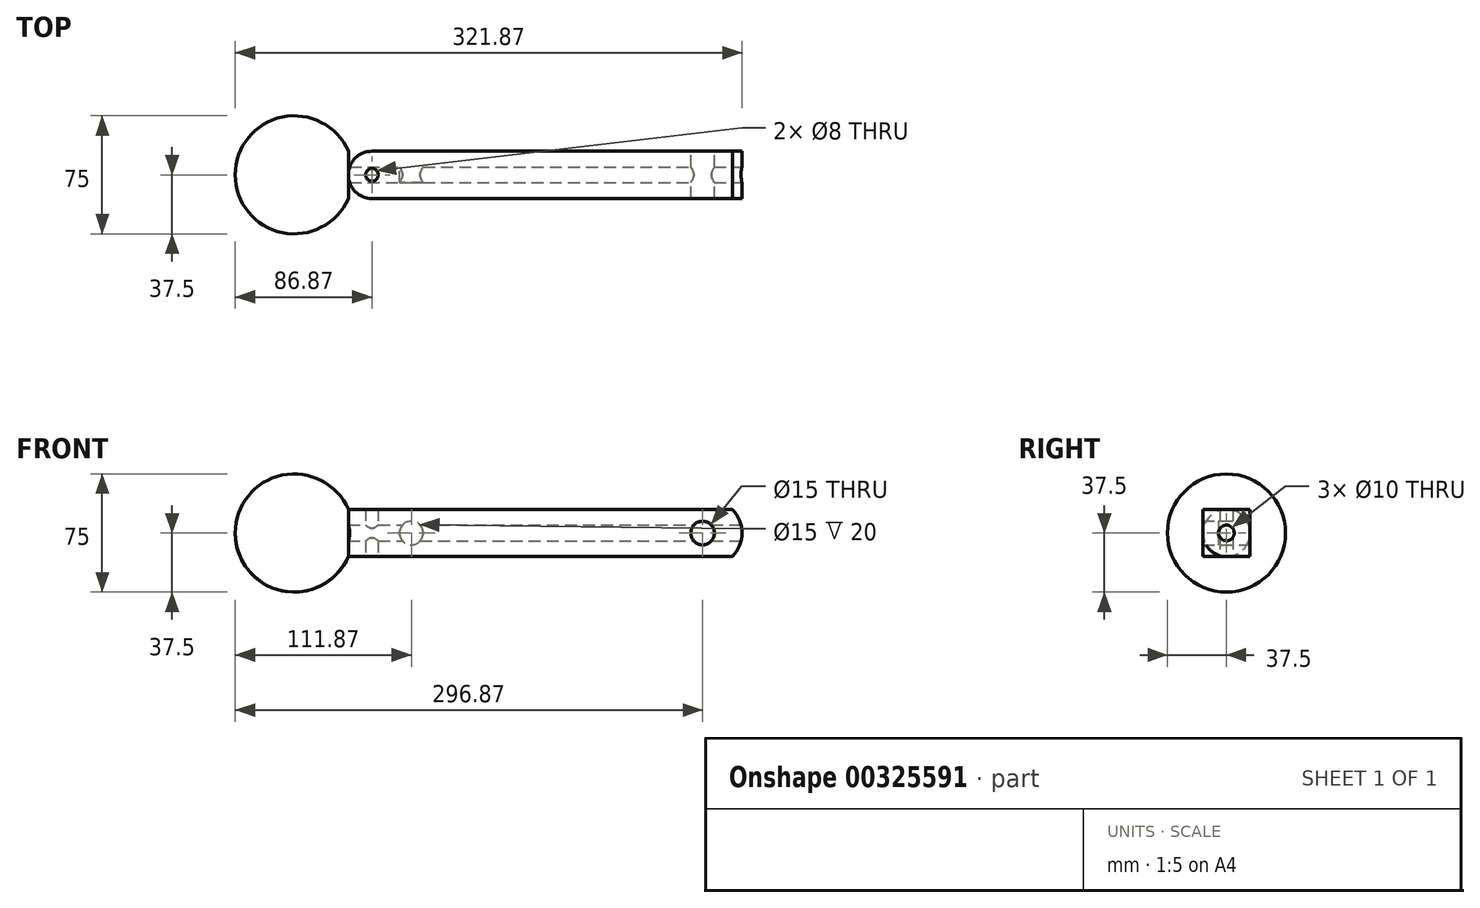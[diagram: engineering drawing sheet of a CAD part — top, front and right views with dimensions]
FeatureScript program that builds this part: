
annotation { "Feature Type Name" : "Feature", "Feature Type Description" : "" }
export const myFeature = defineFeature(function(context is Context, id is Id, definition is map)
    precondition{}
    {
        {
            var Q0;
            Q0=qCreatedBy(makeId("Right.planeOp"),FACE);
            var sketch = newSketch(context, id + "F0", { "sketchPlane" : qUnion([Q0])});
            skLineSegment(sketch, "E0.bottom", {"start": v(15, -15) * mm, "end": v(-15, -15) * mm});
            skLineSegment(sketch, "E0.top", {"start": v(15, 15) * mm, "end": v(-15, 15) * mm});
            skLineSegment(sketch, "E0.left", {"start": v(15, -15) * mm, "end": v(15, 15) * mm});
            skLineSegment(sketch, "E0.right", {"start": v(-15, -15) * mm, "end": v(-15, 15) * mm});
            skPoint(sketch, "E0.middle", {"position": v(0, 0) * mm});
            skSolve(sketch);
        }
        {
            var Q0;
            Q0=makeQuery(id+"F0.imprint","IMPRINT",FACE,{"disambiguationData":[TD([[makeQuery(id+"F0.imprint","IMPRINT",EDGE,{"derivedFrom":sQuery(id+"F0.wireOp",EDGE,"E0.bottom")}),-1.0]])]});
            var Q1;
            Q1 = qConstructionFilter(qBodyType(qCreatedBy(id + "F0" ,EDGE), BodyType.WIRE), ConstructionObject.NO);
            extrude(context, id + "F1", {"entities" : qUnion([Q0]), "surfaceEntities" : qUnion([Q1]), "depth" : 250 * mm});
        }
        {
            var Q0;
            Q0=qCreatedBy(makeId("Front.planeOp"),FACE);
            var sketch = newSketch(context, id + "F2", { "sketchPlane" : qUnion([Q0])});
            skPoint(sketch, "E1", {"position": v(0, 15) * mm});
            skArc(sketch, "E2", {"start": v(3.13, 0) * mm, "mid": v(-34.37, 37.5) * mm, "end": v(-71.87, 0) * mm});
            skLineSegment(sketch, "E3", {"start": v(-81.64, 0) * mm, "end": v(14.73, 0) * mm});
            skSolve(sketch);
        }
        {
            var Q0;
            Q0=makeQuery(id+"F1.opExtrude","SWEPT_FACE",FACE,{"disambiguationData":[OSD([sQuery(id+"F0.wireOp",EDGE,"E0.right")])]});
            var sketch = newSketch(context, id + "F3", { "sketchPlane" : qUnion([Q0])});
            skCircle(sketch, "E4", {"center": v(225, 0) * mm, "radius": 7.5 * mm});
            skSolve(sketch);
        }
        {
            var Q0;
            Q0=makeQuery(id+"F3.imprint","IMPRINT",FACE,{"disambiguationData":[TD([[makeQuery(id+"F3.imprint","IMPRINT",EDGE,{"derivedFrom":sQuery(id+"F3.wireOp",EDGE,"E4")}),1.0]])]});
            extrude(context, id + "F4", {"entities" : qUnion([Q0]), "operationType" : NewBodyOperationType.REMOVE, "endBound" : BoundingType.SYMMETRIC, "depth" : 500 * mm});
        }
        {
            var Q0;
            Q0=makeQuery(id+"F1.opExtrude","CAP_FACE",FACE,{"disambiguationData":[OSD([sQuery(id+"F0.wireOp",EDGE,"E0.bottom"),sQuery(id+"F0.wireOp",EDGE,"E0.top"),sQuery(id+"F0.wireOp",EDGE,"E0.left"),sQuery(id+"F0.wireOp",EDGE,"E0.right")])],"isStart":false});
            var sketch = newSketch(context, id + "F5", { "sketchPlane" : qUnion([Q0])});
            skCircle(sketch, "E5", {"center": v(0, 0) * mm, "radius": 5 * mm});
            skSolve(sketch);
        }
        {
            var Q0;
            Q0=makeQuery(id+"F5.imprint","IMPRINT",FACE,{"disambiguationData":[TD([[makeQuery(id+"F5.imprint","IMPRINT",EDGE,{"derivedFrom":sQuery(id+"F5.wireOp",EDGE,"E5")}),1.0]])]});
            var Q1;
            Q1=qCreatedBy(makeId("Right.planeOp"),FACE);
            extrude(context, id + "F6", {"entities" : qUnion([Q0]), "operationType" : NewBodyOperationType.REMOVE, "oppositeDirection" : true, "endBoundEntityFace" : qUnion([Q1]), "depth" : 280 * mm});
        }
        {
            var Q0;
            Q0=makeQuery(id+"F1.opExtrude","SWEPT_FACE",FACE,{"disambiguationData":[OSD([sQuery(id+"F0.wireOp",EDGE,"E0.left")])]});
            var sketch = newSketch(context, id + "F7", { "sketchPlane" : qUnion([Q0])});
            skCircle(sketch, "E6", {"center": v(-40, 0) * mm, "radius": 7.5 * mm});
            skSolve(sketch);
        }
        {
            var Q0;
            Q0=makeQuery(id+"F7.imprint","IMPRINT",FACE,{"disambiguationData":[TD([[makeQuery(id+"F7.imprint","IMPRINT",EDGE,{"derivedFrom":sQuery(id+"F7.wireOp",EDGE,"E6")}),1.0]])]});
            extrude(context, id + "F8", {"entities" : qUnion([Q0]), "operationType" : NewBodyOperationType.REMOVE, "oppositeDirection" : true, "depth" : 20 * mm});
        }
        {
            var Q0;
            Q0=makeQuery(id+"F1.opExtrude","SWEPT_FACE",FACE,{"disambiguationData":[OSD([sQuery(id+"F0.wireOp",EDGE,"E0.left")])]});
            var sketch = newSketch(context, id + "F9", { "sketchPlane" : qUnion([Q0])});
            skCircle(sketch, "E7", {"center": v(-228.5, 0) * mm, "radius": 21.5 * mm});
            skSolve(sketch);
        }
        {
            var Q0;
            {var subQ0=sQuery(id+"F9.wireOp",EDGE,"E7");var subQ1=sQuery(id+"F0.wireOp",EDGE,"E0.left");var subQ4=makeQuery(id+"F1.opExtrude","CAP_EDGE",EDGE,{"disambiguationData":[OSD([subQ1])],"isStart":false});var subQ5=makeQuery(id+"F9.imprint","INTERSECT",VERTEX,{"derivedFrom":[subQ4,subQ0]});Q0=makeQuery(id+"F9.imprint","IMPRINT",FACE,{"disambiguationData":[TD([[makeQuery(id+"F9.imprint","IMPRINT",EDGE,{"disambiguationData":[TD([[subQ5,1.0]])],"derivedFrom":subQ0}),-1.0]])]});}
            var Q1;
            {var subQ0=sQuery(id+"F9.wireOp",EDGE,"E7");var subQ1=sQuery(id+"F0.wireOp",EDGE,"E0.left");var subQ2=makeQuery(id+"F1.opExtrude","CAP_EDGE",EDGE,{"disambiguationData":[OSD([subQ1])],"isStart":false});var subQ3=makeQuery(id+"F9.imprint","INTERSECT",VERTEX,{"derivedFrom":[subQ2,subQ0]});Q1=makeQuery(id+"F9.imprint","IMPRINT",FACE,{"disambiguationData":[TD([[makeQuery(id+"F9.imprint","IMPRINT",EDGE,{"disambiguationData":[TD([[subQ3,-1.0]])],"derivedFrom":subQ0}),-1.0]])]});}
            extrude(context, id + "F10", {"entities" : qUnion([Q0, Q1]), "operationType" : NewBodyOperationType.REMOVE, "endBound" : BoundingType.THROUGH_ALL, "oppositeDirection" : true, "depth" : 25 * mm});
        }
        {
            var Q0;
            Q0=makeQuery(id+"F2.imprint","IMPRINT",FACE,{"disambiguationData":[TD([[makeQuery(id+"F2.imprint","IMPRINT",EDGE,{"derivedFrom":sQuery(id+"F2.wireOp",EDGE,"E2")}),1.0]])]});
            var Q1;
            Q1=sQuery(id+"F2.wireOp",EDGE,"E3");
            revolve(context, id + "F11", {"entities" : qUnion([Q0]), "axis" : qUnion([Q1]), "revolveType" : RevolveType.FULL});
        }
        {
            var Q0;
            Q0=makeQuery(id+"F1.opExtrude","SWEPT_FACE",FACE,{"disambiguationData":[OSD([sQuery(id+"F0.wireOp",EDGE,"E0.bottom")])]});
            var sketch = newSketch(context, id + "F12", { "sketchPlane" : qUnion([Q0])});
            skCircle(sketch, "E8", {"center": v(15, 0) * mm, "radius": 4 * mm});
            skCircle(sketch, "E9", {"center": v(15, 0) * mm, "radius": 15 * mm});
            skSolve(sketch);
        }
        {
            var Q0;
            Q0=makeQuery(id+"F12.imprint","IMPRINT",FACE,{"disambiguationData":[TD([[makeQuery(id+"F12.imprint","IMPRINT",EDGE,{"derivedFrom":sQuery(id+"F12.wireOp",EDGE,"E8")}),1.0]])]});
            var Q1;
            {var subQ0=sQuery(id+"F12.wireOp",EDGE,"E9");var subQ1=sQuery(id+"F0.wireOp",EDGE,"E0.bottom");var subQ2=makeQuery(id+"F1.opExtrude","CAP_EDGE",EDGE,{"disambiguationData":[OSD([subQ1])],"isStart":true});var subQ3=makeQuery(id+"F12.imprint","INTERSECT",VERTEX,{"derivedFrom":[subQ2,subQ0]});Q1=makeQuery(id+"F12.imprint","IMPRINT",FACE,{"disambiguationData":[TD([[makeQuery(id+"F12.imprint","IMPRINT",EDGE,{"disambiguationData":[TD([[subQ3,-1.0]])],"derivedFrom":subQ0}),-1.0]])]});}
            var Q2;
            {var subQ0=sQuery(id+"F12.wireOp",EDGE,"E9");var subQ1=sQuery(id+"F0.wireOp",EDGE,"E0.bottom");var subQ2=makeQuery(id+"F1.opExtrude","CAP_EDGE",EDGE,{"disambiguationData":[OSD([subQ1])],"isStart":true});var subQ3=makeQuery(id+"F12.imprint","INTERSECT",VERTEX,{"derivedFrom":[subQ2,subQ0]});Q2=makeQuery(id+"F12.imprint","IMPRINT",FACE,{"disambiguationData":[TD([[makeQuery(id+"F12.imprint","IMPRINT",EDGE,{"disambiguationData":[TD([[subQ3,1.0]])],"derivedFrom":subQ0}),-1.0]])]});}
            extrude(context, id + "F13", {"entities" : qUnion([Q0, Q1, Q2]), "operationType" : NewBodyOperationType.REMOVE, "endBound" : BoundingType.THROUGH_ALL, "oppositeDirection" : true, "depth" : 25 * mm});
        }
    });
